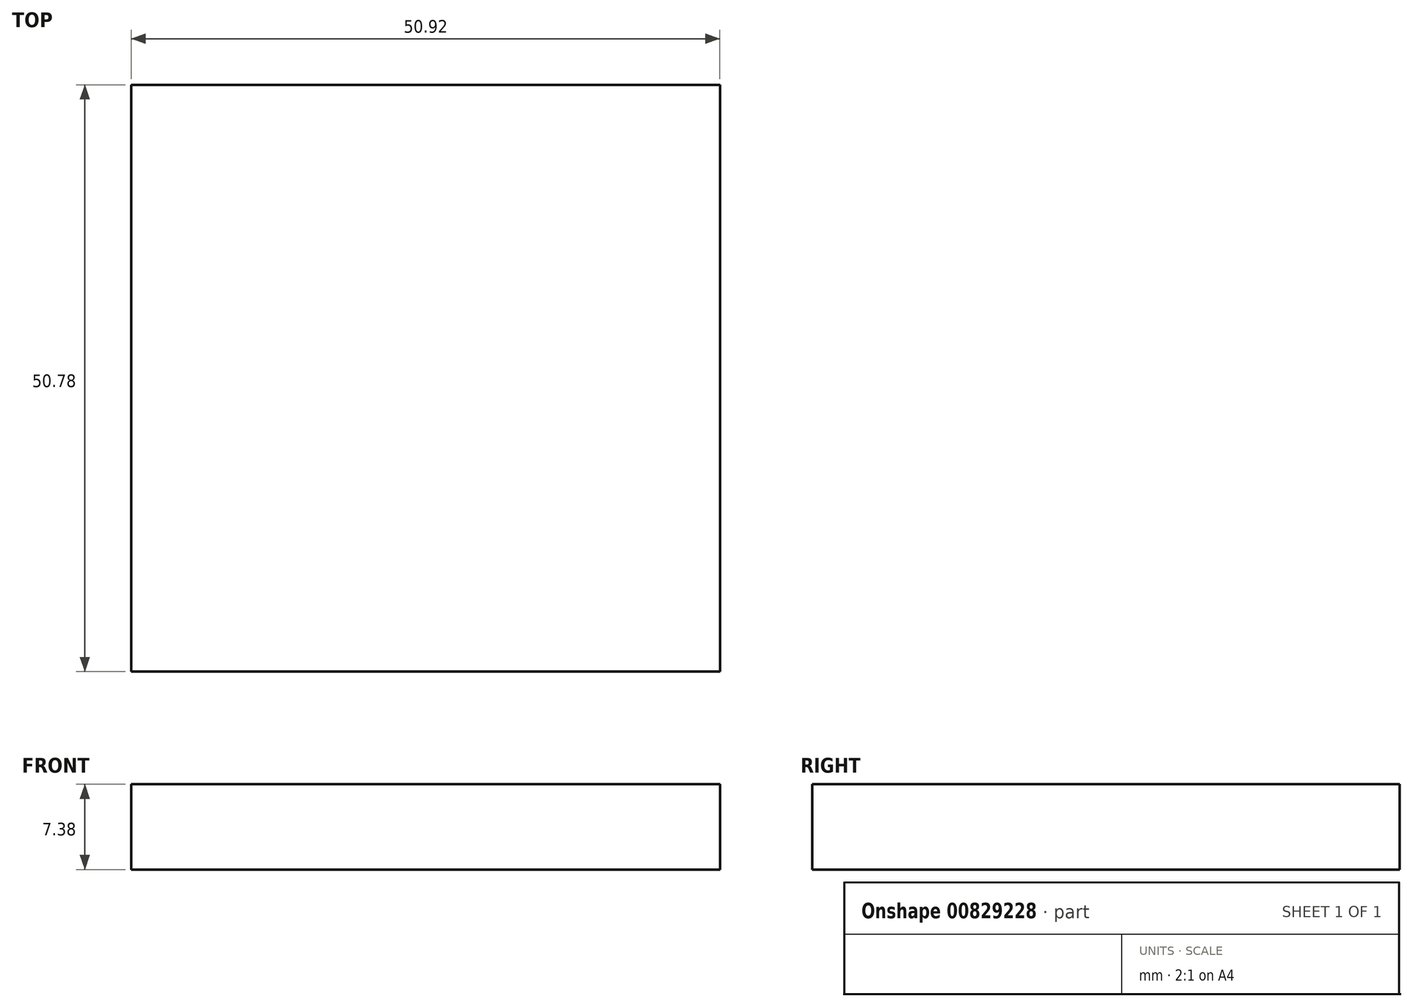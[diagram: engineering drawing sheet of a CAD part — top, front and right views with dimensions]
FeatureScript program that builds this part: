
annotation { "Feature Type Name" : "Feature", "Feature Type Description" : "" }
export const myFeature = defineFeature(function(context is Context, id is Id, definition is map)
    precondition{}
    {
        {
            var Q0;
            Q0=qCreatedBy(makeId("Top.planeOp"),FACE);
            var sketch = newSketch(context, id + "F0", { "sketchPlane" : qUnion([Q0])});
            skLineSegment(sketch, "E0.bottom", {"start": v(-25.46, 25.39) * mm, "end": v(25.46, 25.39) * mm});
            skLineSegment(sketch, "E0.top", {"start": v(-25.46, -25.39) * mm, "end": v(25.46, -25.39) * mm});
            skLineSegment(sketch, "E0.left", {"start": v(-25.46, 25.39) * mm, "end": v(-25.46, -25.39) * mm});
            skLineSegment(sketch, "E0.right", {"start": v(25.46, 25.39) * mm, "end": v(25.46, -25.39) * mm});
            skPoint(sketch, "E0.middle", {"position": v(0, 0) * mm});
            skSolve(sketch);
        }
        {
            var Q0;
            Q0 = qSketchRegion(id + "F0", true);
            extrude(context, id + "F1", {"entities" : qUnion([Q0]), "depth" : 7.38 * mm, "offsetDistance" : 25.4 * mm});
        }
        {
            var Q0;
            Q0=makeQuery(id+"F1.opExtrude","SWEPT_FACE",FACE,{"disambiguationData":[OSD([sQuery(id+"F0.wireOp",EDGE,"E0.top")])]});
            var sketch = newSketch(context, id + "F2", { "sketchPlane" : qUnion([Q0])});
            skLineSegment(sketch, "E1.0", {"start": v(25.46, 7.38) * mm, "end": v(25.46, 0) * mm});
            skSolve(sketch);
        }
    });
